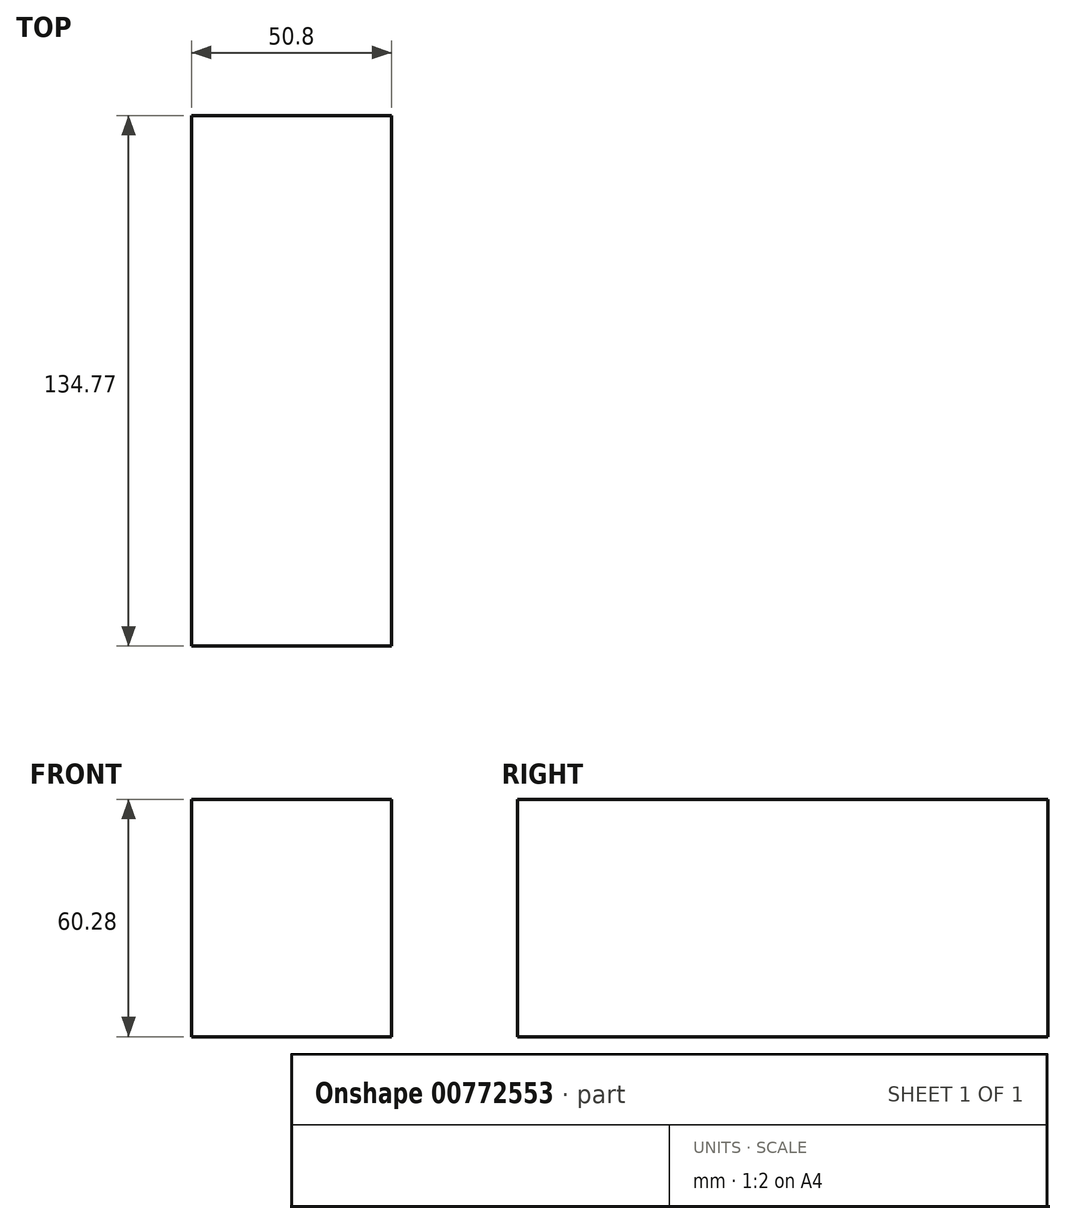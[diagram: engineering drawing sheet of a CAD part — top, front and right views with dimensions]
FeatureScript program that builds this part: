
annotation { "Feature Type Name" : "Feature", "Feature Type Description" : "" }
export const myFeature = defineFeature(function(context is Context, id is Id, definition is map)
    precondition{}
    {
        {
            var Q0;
            Q0=qCreatedBy(makeId("Right.planeOp"),FACE);
            var sketch = newSketch(context, id + "F0", { "sketchPlane" : qUnion([Q0])});
            skLineSegment(sketch, "E0.bottom", {"start": v(-57.92, 23.67) * mm, "end": v(76.85, 23.67) * mm});
            skLineSegment(sketch, "E0.top", {"start": v(-57.92, -36.61) * mm, "end": v(76.85, -36.61) * mm});
            skLineSegment(sketch, "E0.left", {"start": v(-57.92, 23.67) * mm, "end": v(-57.92, -36.61) * mm});
            skLineSegment(sketch, "E0.right", {"start": v(76.85, 23.67) * mm, "end": v(76.85, -36.61) * mm});
            skSolve(sketch);
        }
        {
            var Q0;
            Q0=makeQuery(id+"F0.imprint","IMPRINT",FACE,{"disambiguationData":[TD([[makeQuery(id+"F0.imprint","IMPRINT",EDGE,{"derivedFrom":sQuery(id+"F0.wireOp",EDGE,"E0.bottom")}),-1.0]])]});
            extrude(context, id + "F1", {"entities" : qUnion([Q0]), "depth" : 50.8 * mm, "offsetDistance" : 25.4 * mm});
        }
    });
